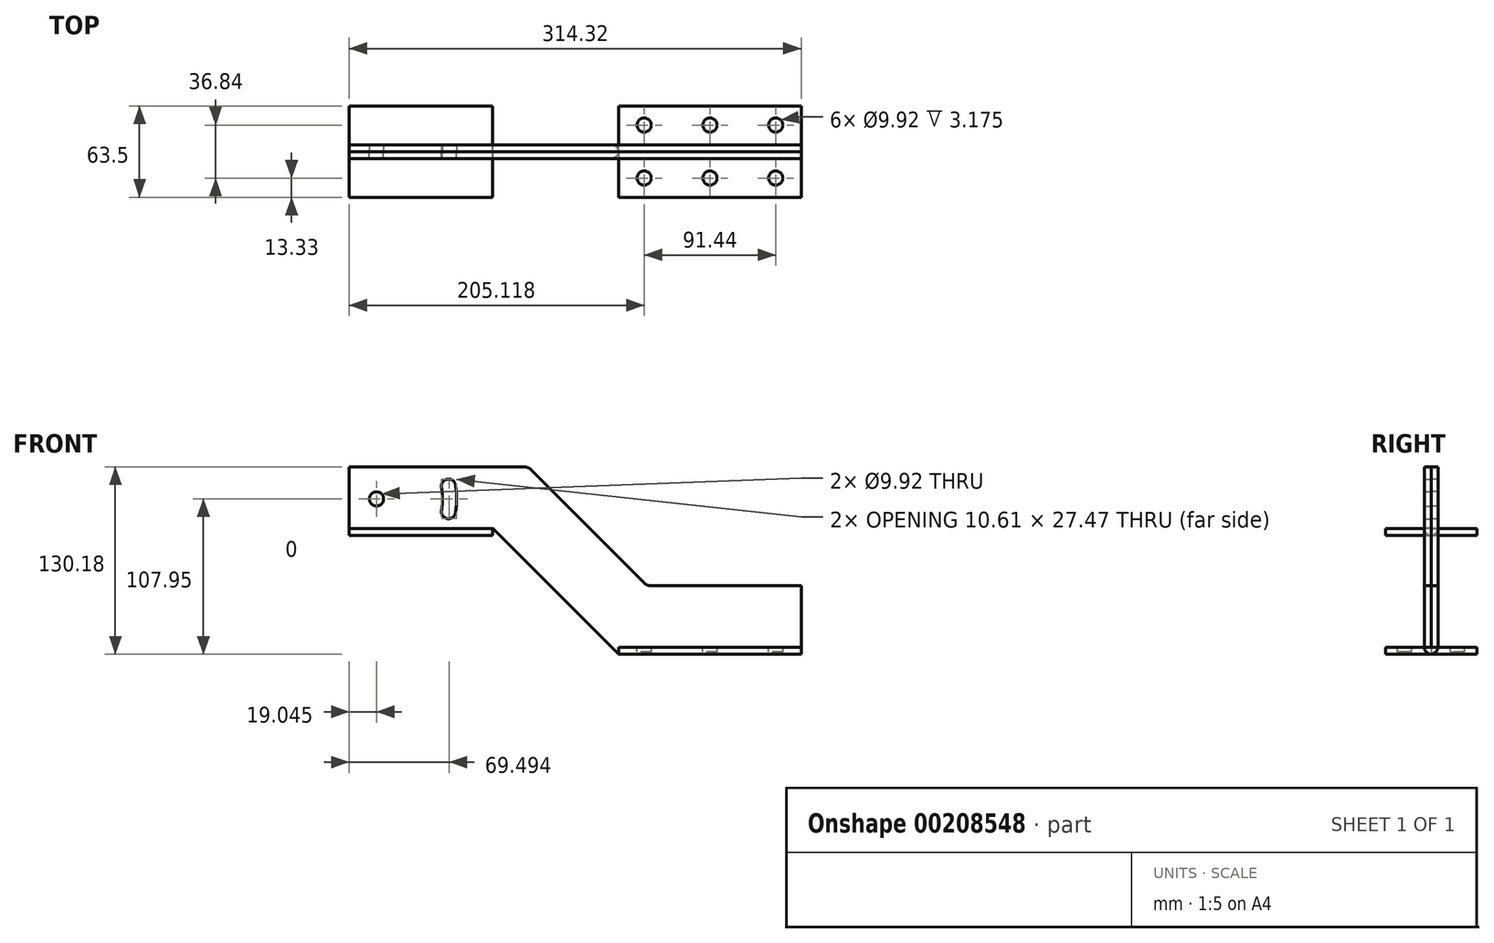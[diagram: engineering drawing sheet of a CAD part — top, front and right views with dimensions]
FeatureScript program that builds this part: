
annotation { "Feature Type Name" : "Feature", "Feature Type Description" : "" }
export const myFeature = defineFeature(function(context is Context, id is Id, definition is map)
    precondition{}
    {
        {
            var Q0;
            Q0=qCreatedBy(makeId("Front.planeOp"),FACE);
            var sketch = newSketch(context, id + "F0", { "sketchPlane" : qUnion([Q0])});
            skLineSegment(sketch, "E0", {"start": v(0, 0) * mm, "end": v(127, 0) * mm});
            skLineSegment(sketch, "E1", {"start": v(0, 0) * mm, "end": v(-82.55, 82.55) * mm});
            skLineSegment(sketch, "E2", {"start": v(-82.55, 82.55) * mm, "end": v(-187.33, 82.55) * mm});
            skLineSegment(sketch, "E3.0", {"start": v(-65.45, 130.17) * mm, "end": v(-187.33, 130.17) * mm});
            skLineSegment(sketch, "E3.1", {"start": v(17.87, 49.48) * mm, "end": v(-60.96, 128.32) * mm});
            skLineSegment(sketch, "E3.2", {"start": v(22.36, 47.63) * mm, "end": v(127, 47.63) * mm});
            skLineSegment(sketch, "E4", {"start": v(-187.33, 130.17) * mm, "end": v(-187.33, 82.55) * mm});
            skLineSegment(sketch, "E5", {"start": v(127, 47.62) * mm, "end": v(127, 0) * mm});
            skCircle(sketch, "E6", {"center": v(-168.28, 107.95) * mm, "radius": 4.96 * mm});
            skLineSegment(sketch, "E7.direction1", {"start": v(-168.28, 107.95) * mm, "end": v(-117.47, 107.95) * mm, "construction": true});
            skPoint(sketch, "E8.visualSharp", {"position": v(-62.82, 130.17) * mm});
            skArc(sketch, "E8.filletArc", {"start": v(-60.96, 128.32) * mm, "mid": v(-63.02, 129.7) * mm, "end": v(-65.45, 130.17) * mm});
            skPoint(sketch, "E9.visualSharp", {"position": v(19.73, 47.63) * mm});
            skArc(sketch, "E9.filletArc", {"start": v(17.87, 49.48) * mm, "mid": v(19.93, 48.1) * mm, "end": v(22.36, 47.63) * mm});
            skPoint(sketch, "E10.visualSharp", {"position": v(-82.55, 82.55) * mm});
            skPoint(sketch, "E11.visualSharp", {"position": v(-187.33, 130.17) * mm});
            skPoint(sketch, "E12.visualSharp", {"position": v(-187.33, 82.55) * mm});
            skPoint(sketch, "E13.visualSharp", {"position": v(127, 47.63) * mm});
            skPoint(sketch, "E14.visualSharp", {"position": v(127, 0) * mm});
            skArc(sketch, "E15", {"start": v(-117.47, 107.95) * mm, "mid": v(-117.67, 112.4) * mm, "end": v(-118.25, 116.8) * mm, "construction": true});
            skArc(sketch, "E16", {"start": v(-117.47, 107.95) * mm, "mid": v(-117.67, 103.5) * mm, "end": v(-118.25, 99.1) * mm, "construction": true});
            skArc(sketch, "E17.0", {"start": v(-112.52, 107.95) * mm, "mid": v(-112.74, 112.83) * mm, "end": v(-113.38, 117.67) * mm});
            skArc(sketch, "E17.1", {"start": v(-112.52, 107.95) * mm, "mid": v(-112.74, 103.07) * mm, "end": v(-113.38, 98.23) * mm});
            skArc(sketch, "E18.0", {"start": v(-122.43, 107.95) * mm, "mid": v(-122.6, 111.96) * mm, "end": v(-123.13, 115.94) * mm});
            skArc(sketch, "E18.1", {"start": v(-122.43, 107.95) * mm, "mid": v(-122.6, 103.94) * mm, "end": v(-123.13, 99.96) * mm});
            skArc(sketch, "E19", {"start": v(-123.13, 115.94) * mm, "mid": v(-119.12, 121.68) * mm, "end": v(-113.38, 117.67) * mm});
            skArc(sketch, "E20", {"start": v(-123.13, 99.96) * mm, "mid": v(-119.12, 94.22) * mm, "end": v(-113.38, 98.23) * mm});
            skSolve(sketch);
        }
        {
            var Q0;
            Q0=makeQuery(id+"F0.imprint","IMPRINT",FACE,{"disambiguationData":[TD([[makeQuery(id+"F0.imprint","IMPRINT",EDGE,{"derivedFrom":sQuery(id+"F0.wireOp",EDGE,"E0")}),1.0]])]});
            extrude(context, id + "F1", {"entities" : qUnion([Q0]), "depth" : 4.76 * mm});
        }
        {
            var Q0;
            Q0=makeQuery(id+"F1.opExtrude","SWEPT_FACE",FACE,{"disambiguationData":[OSD([sQuery(id+"F0.wireOp",EDGE,"E5")])]});
            var sketch = newSketch(context, id + "F2", { "sketchPlane" : qUnion([Q0])});
            skLineSegment(sketch, "E21.bottom", {"start": v(0, 0) * mm, "end": v(31.75, 0) * mm});
            skLineSegment(sketch, "E21.top", {"start": v(0, 4.76) * mm, "end": v(31.75, 4.76) * mm});
            skLineSegment(sketch, "E21.left", {"start": v(0, 0) * mm, "end": v(0, 4.76) * mm});
            skLineSegment(sketch, "E21.right", {"start": v(31.75, 0) * mm, "end": v(31.75, 4.76) * mm});
            skSolve(sketch);
        }
        {
            var Q0;
            Q0=qSketchRegion(id+"F2",true);
            extrude(context, id + "F3", {"entities" : qUnion([Q0]), "operationType" : NewBodyOperationType.ADD, "oppositeDirection" : true, "depth" : 127 * mm});
        }
        {
            var Q0;
            Q0=makeQuery(id+"F1.opExtrude","CAP_EDGE",EDGE,{"disambiguationData":[OSD([sQuery(id+"F0.wireOp",EDGE,"E0")])],"isStart":false});
            var Q1;
            Q1=makeQuery(id+"F3.opExtrude","SWEPT_EDGE",EDGE,{"disambiguationData":[OSD([sQuery(id+"F0.wireOp",EDGE,"E5"),sQuery(id+"F2.wireOp",EDGE,"E21.top"),sQuery(id+"F2.wireOp",EDGE,"E21.left")])]});
            fillet(context, id + "F4", {"entities" : qUnion([Q0, Q1]), "radius" : 5.08 * mm, "tangentPropagation" : true, "allowEdgeOverflow" : false});
        }
        {
            var Q0;
            Q0=makeQuery(id+"F3.opExtrude","SWEPT_FACE",FACE,{"disambiguationData":[OSD([sQuery(id+"F2.wireOp",EDGE,"E21.top")])]});
            var sketch = newSketch(context, id + "F5", { "sketchPlane" : qUnion([Q0])});
            skCircle(sketch, "E22", {"center": v(17.8, 18.42) * mm, "radius": 4.96 * mm});
            skCircle(sketch, "E23.1.0.0", {"center": v(63.52, 18.42) * mm, "radius": 4.96 * mm});
            skCircle(sketch, "E23.2.0.0", {"center": v(109.24, 18.42) * mm, "radius": 4.96 * mm});
            skLineSegment(sketch, "E23.direction1", {"start": v(17.8, 18.42) * mm, "end": v(63.52, 18.42) * mm, "construction": true});
            skSolve(sketch);
        }
        {
            var Q0;
            Q0=qSketchRegion(id+"F5",true);
            extrude(context, id + "F6", {"entities" : qUnion([Q0]), "operationType" : NewBodyOperationType.REMOVE, "oppositeDirection" : true, "depth" : 3.17 * mm});
        }
        {
            var Q0;
            Q0=makeQuery(id+"F1.opExtrude","SWEPT_FACE",FACE,{"disambiguationData":[OSD([sQuery(id+"F0.wireOp",EDGE,"E4")])]});
            var sketch = newSketch(context, id + "F7", { "sketchPlane" : qUnion([Q0])});
            skLineSegment(sketch, "E24.bottom", {"start": v(0, 82.55) * mm, "end": v(-31.75, 82.55) * mm});
            skLineSegment(sketch, "E24.top", {"start": v(0, 87.31) * mm, "end": v(-31.75, 87.31) * mm});
            skLineSegment(sketch, "E24.left", {"start": v(0, 82.55) * mm, "end": v(0, 87.31) * mm});
            skLineSegment(sketch, "E24.right", {"start": v(-31.75, 82.55) * mm, "end": v(-31.75, 87.31) * mm});
            skSolve(sketch);
        }
        {
            var Q0;
            Q0=qSketchRegion(id+"F7",true);
            extrude(context, id + "F8", {"entities" : qUnion([Q0]), "operationType" : NewBodyOperationType.ADD, "oppositeDirection" : true, "depth" : 99.7 * mm});
        }
        {
            var Q0;
            Q0=makeQuery(id+"F1.opExtrude","CAP_EDGE",EDGE,{"disambiguationData":[OSD([sQuery(id+"F0.wireOp",EDGE,"E2")])],"isStart":false});
            var Q1;
            Q1=makeQuery(id+"F8.opExtrude","SWEPT_EDGE",EDGE,{"disambiguationData":[OSD([sQuery(id+"F0.wireOp",EDGE,"E4"),sQuery(id+"F7.wireOp",EDGE,"E24.top"),sQuery(id+"F7.wireOp",EDGE,"E24.left")])]});
            fillet(context, id + "F9", {"entities" : qUnion([Q0, Q1]), "radius" : 5.08 * mm, "tangentPropagation" : true, "allowEdgeOverflow" : false});
        }
        {
            var Q0;
            Q0=makeQuery(id+"F1.opExtrude","CAP_FACE",FACE,{"disambiguationData":[OSD([sQuery(id+"F0.wireOp",EDGE,"E0"),sQuery(id+"F0.wireOp",EDGE,"E1"),sQuery(id+"F0.wireOp",EDGE,"E2"),sQuery(id+"F0.wireOp",EDGE,"E3.0"),sQuery(id+"F0.wireOp",EDGE,"E3.1"),sQuery(id+"F0.wireOp",EDGE,"E3.2"),sQuery(id+"F0.wireOp",EDGE,"E4"),sQuery(id+"F0.wireOp",EDGE,"E5"),sQuery(id+"F0.wireOp",EDGE,"E6"),sQuery(id+"F0.wireOp",EDGE,"E7.1.0.0"),sQuery(id+"F0.wireOp",EDGE,"E8.filletArc"),sQuery(id+"F0.wireOp",EDGE,"E9.filletArc")])],"isStart":false});
            var sketch = newSketch(context, id + "F10", { "sketchPlane" : qUnion([Q0])});
            skLineSegment(sketch, "E25", {"start": v(-87.63, 87.63) * mm, "end": v(-87.63, 82.56) * mm});
            skLineSegment(sketch, "E26", {"start": v(-87.63, 82.56) * mm, "end": v(-82.56, 82.56) * mm});
            skLineSegment(sketch, "E27", {"start": v(-82.56, 82.56) * mm, "end": v(-87.63, 87.63) * mm});
            skSolve(sketch);
        }
        {
            var Q0;
            Q0=qSketchRegion(id+"F10",true);
            extrude(context, id + "F11", {"entities" : qUnion([Q0]), "operationType" : NewBodyOperationType.REMOVE, "oppositeDirection" : true, "depth" : 25.4 * mm});
        }
        {
            var Q0;
            Q0=makeQuery(id+"F1.opExtrude","SWEPT_BODY",BODY,{"disambiguationData":[OSD([sQuery(id+"F0.wireOp",EDGE,"E0"),sQuery(id+"F0.wireOp",EDGE,"E1"),sQuery(id+"F0.wireOp",EDGE,"E2"),sQuery(id+"F0.wireOp",EDGE,"E3.0"),sQuery(id+"F0.wireOp",EDGE,"E3.1"),sQuery(id+"F0.wireOp",EDGE,"E3.2"),sQuery(id+"F0.wireOp",EDGE,"E4"),sQuery(id+"F0.wireOp",EDGE,"E5"),sQuery(id+"F0.wireOp",EDGE,"E6"),sQuery(id+"F0.wireOp",EDGE,"E8.filletArc"),sQuery(id+"F0.wireOp",EDGE,"E9.filletArc"),sQuery(id+"F0.wireOp",EDGE,"E17.0"),sQuery(id+"F0.wireOp",EDGE,"E17.1"),sQuery(id+"F0.wireOp",EDGE,"E18.0"),sQuery(id+"F0.wireOp",EDGE,"E18.1"),sQuery(id+"F0.wireOp",EDGE,"E19"),sQuery(id+"F0.wireOp",EDGE,"E20")])]});
            var Q1;
            Q1=qCreatedBy(makeId("Front.planeOp"),FACE);
            mirror(context, id + "F12", {"entities" : qUnion([Q0]), "mirrorPlane" : qUnion([Q1])});
        }
    });
